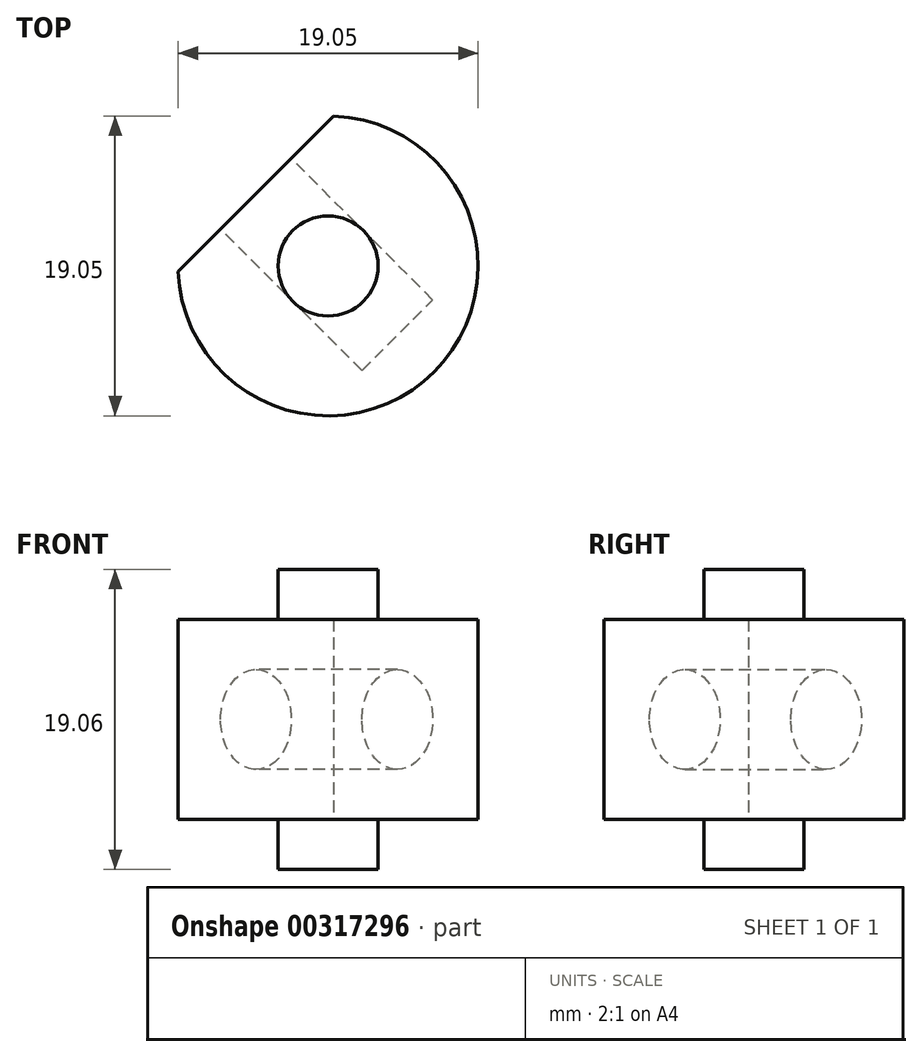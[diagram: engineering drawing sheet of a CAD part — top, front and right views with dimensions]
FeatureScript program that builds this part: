
annotation { "Feature Type Name" : "Feature", "Feature Type Description" : "" }
export const myFeature = defineFeature(function(context is Context, id is Id, definition is map)
    precondition{}
    {
        {
            var Q0;
            Q0=qCreatedBy(makeId("Top.planeOp"),FACE);
            var sketch = newSketch(context, id + "F0", { "sketchPlane" : qUnion([Q0])});
            skCircle(sketch, "E0", {"center": v(0, 0) * mm, "radius": 9.53 * mm});
            skSolve(sketch);
        }
        {
            var Q0;
            Q0=qSketchRegion(id+"F0",true);
            extrude(context, id + "F1", {"entities" : qUnion([Q0]), "depth" : 12.7 * mm});
        }
        {
            var Q0;
            Q0=makeQuery(id+"F1.opExtrude","CAP_FACE",FACE,{"disambiguationData":[OSD([sQuery(id+"F0.wireOp",EDGE,"E0")])],"isStart":false});
            var sketch = newSketch(context, id + "F2", { "sketchPlane" : qUnion([Q0])});
            skCircle(sketch, "E1", {"center": v(0, 0) * mm, "radius": 3.18 * mm});
            skSolve(sketch);
        }
        {
            var Q0;
            Q0=qSketchRegion(id+"F2",true);
            extrude(context, id + "F3", {"entities" : qUnion([Q0]), "operationType" : NewBodyOperationType.ADD, "depth" : 3.17 * mm});
        }
        {
            var Q0;
            Q0=makeQuery(id+"F1.opExtrude","CAP_FACE",FACE,{"disambiguationData":[OSD([sQuery(id+"F0.wireOp",EDGE,"E0")])],"isStart":true});
            var sketch = newSketch(context, id + "F4", { "sketchPlane" : qUnion([Q0])});
            skCircle(sketch, "E2", {"center": v(0, 0) * mm, "radius": 3.17 * mm});
            skSolve(sketch);
        }
        {
            var Q0;
            Q0=qSketchRegion(id+"F4",true);
            extrude(context, id + "F5", {"entities" : qUnion([Q0]), "operationType" : NewBodyOperationType.ADD, "depth" : 3.17 * mm});
        }
        {
            var Q0;
            Q0=makeQuery(id+"F1.opExtrude","CAP_FACE",FACE,{"disambiguationData":[OSD([sQuery(id+"F0.wireOp",EDGE,"E0")])],"isStart":true});
            var sketch = newSketch(context, id + "F6", { "sketchPlane" : qUnion([Q0])});
            skLineSegment(sketch, "E3", {"start": v(0, 0) * mm, "end": v(0, -9.53) * mm});
            skLineSegment(sketch, "E4", {"start": v(0, 0) * mm, "end": v(-9.53, 0) * mm});
            skLineSegment(sketch, "E5", {"start": v(-4.58, -4.58) * mm, "end": v(-9.52, 0.36) * mm});
            skLineSegment(sketch, "E6", {"start": v(-4.58, -4.58) * mm, "end": v(0.36, -9.52) * mm});
            skSolve(sketch);
        }
        {
            var Q0;
            {var subQ0=sQuery(id+"F6.wireOp",EDGE,"E3");var subQ1=makeQuery(id+"F1.opExtrude","CAP_EDGE",EDGE,{"disambiguationData":[OSD([sQuery(id+"F0.wireOp",EDGE,"E0")])],"isStart":true});var subQ2=makeQuery(id+"F6.imprint","INTERSECT",VERTEX,{"derivedFrom":[subQ1,subQ0]});Q0=makeQuery(id+"F6.imprint","IMPRINT",FACE,{"disambiguationData":[TD([[makeQuery(id+"F6.imprint","IMPRINT",EDGE,{"disambiguationData":[TD([[subQ2,1.0]])],"derivedFrom":subQ0}),1.0]])]});}
            var Q1;
            {var subQ3=sQuery(id+"F6.wireOp",EDGE,"E3");var subQ7=makeQuery(id+"F1.opExtrude","CAP_EDGE",EDGE,{"disambiguationData":[OSD([sQuery(id+"F0.wireOp",EDGE,"E0")])],"isStart":true});var subQ9=makeQuery(id+"F6.imprint","INTERSECT",VERTEX,{"derivedFrom":[subQ7,subQ3]});Q1=makeQuery(id+"F6.imprint","IMPRINT",FACE,{"disambiguationData":[TD([[makeQuery(id+"F6.imprint","IMPRINT",EDGE,{"disambiguationData":[TD([[subQ9,1.0]])],"derivedFrom":subQ3}),-1.0]])]});}
            var Q2;
            {var subQ0=sQuery(id+"F6.wireOp",EDGE,"E4");var subQ1=makeQuery(id+"F1.opExtrude","CAP_EDGE",EDGE,{"disambiguationData":[OSD([sQuery(id+"F0.wireOp",EDGE,"E0")])],"isStart":true});var subQ2=makeQuery(id+"F6.imprint","INTERSECT",VERTEX,{"derivedFrom":[subQ1,subQ0]});Q2=makeQuery(id+"F6.imprint","IMPRINT",FACE,{"disambiguationData":[TD([[makeQuery(id+"F6.imprint","IMPRINT",EDGE,{"disambiguationData":[TD([[subQ2,1.0]])],"derivedFrom":subQ0}),-1.0]])]});}
            extrude(context, id + "F7", {"entities" : qUnion([Q0, Q1, Q2]), "operationType" : NewBodyOperationType.REMOVE, "oppositeDirection" : true, "depth" : 25.4 * mm});
        }
        {
            var Q0;
            Q0=makeQuery(id+"F7.boolean.opBoolean","COPY",FACE,{"derivedFrom":makeQuery(id+"F7.opExtrude","SWEPT_FACE",FACE,{"disambiguationData":[OSD([sQuery(id+"F6.wireOp",EDGE,"E5"),sQuery(id+"F6.wireOp",EDGE,"E6")])]})});
            var sketch = newSketch(context, id + "F8", { "sketchPlane" : qUnion([Q0])});
            skCircle(sketch, "E7", {"center": v(0, 6.35) * mm, "radius": 3.18 * mm});
            skLineSegment(sketch, "E8", {"start": v(-6.99, 12.7) * mm, "end": v(6.99, 0) * mm, "construction": true});
            skSolve(sketch);
        }
        {
            var Q0;
            Q0=qSketchRegion(id+"F8",true);
            extrude(context, id + "F9", {"entities" : qUnion([Q0]), "operationType" : NewBodyOperationType.REMOVE, "oppositeDirection" : true, "depth" : 12.7 * mm});
        }
    });
